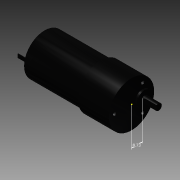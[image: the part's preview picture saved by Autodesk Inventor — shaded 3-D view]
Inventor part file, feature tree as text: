
AUTODESK INVENTOR PART (.ipt)
format: ipt  version: 2015 (Build 190159000, 159)  size: 157,696 bytes
history: native  units: mm
features: sketch x6, revolve x2, extrude x2, hole x1
ambient origin geometry x8: Origin, YZ Plane, XZ Plane, XY Plane, X Axis, Y Axis, Z Axis, Center Point
bodies: Solid1 (feature_tree)
feature tree (11):
  revolve  "Revolution1"  [1 undecoded]
  sketch  "Sketch2"  dims[d2=24.3mm d3=17.7mm]
  revolve  "Revolution2"  [1 undecoded]
  extrude  "Extrusion1"  Depth=8.73mm
  hole  "Hole1"  [1 undecoded]
  extrude  "Extrusion2"  Depth=12.5mm
  sketch  "Sketch1"  dims[d0=16.1mm d1=68.1mm]
  sketch  "Sketch3"  dims[d4=90.0deg d5=8.73mm]
  sketch  "Sketch4"  dims[d6=6.0mm d8=2.5mm]
  sketch  "Sketch5"  dims[d9=1.5mm d10=12.5mm]
  sketch  "Sketch6"  dims[d11=90.0deg d12=1.0mm d13=9.5mm d14=10.0mm d15=0.0mm d16=20.5mm d17=8.73mm d18=22.1mm d19=2.459mm d20=6.0mm d21=4.0mm d22=2.0mm d23=90.0deg d24=4.5mm d25=0.0mm d26=2.8mm d27=0.5mm d28=11.25mm d29=9.5mm d30=0.0mm]
note: 3 required parameter values undecoded (feature->parameter linkage not recoverable at this tier; creation-order binding heuristic only, values carry confidence <= 0.55)